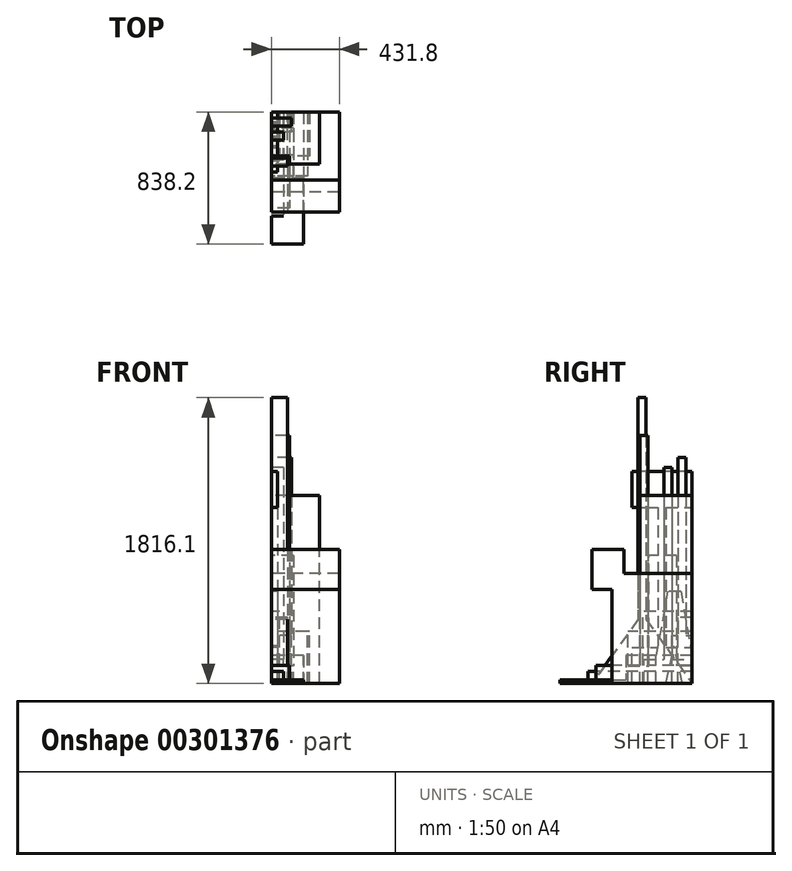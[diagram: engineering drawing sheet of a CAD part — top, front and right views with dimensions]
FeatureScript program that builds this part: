
annotation { "Feature Type Name" : "Feature", "Feature Type Description" : "" }
export const myFeature = defineFeature(function(context is Context, id is Id, definition is map)
    precondition{}
    {
        {
            var Q0;
            Q0=qCreatedBy(makeId("Right.planeOp"),FACE);
            var sketch = newSketch(context, id + "F0", { "sketchPlane" : qUnion([Q0])});
            skLineSegment(sketch, "E0.bottom", {"start": v(0, 0) * mm, "end": v(-508, 0) * mm});
            skLineSegment(sketch, "E0.top", {"start": v(0, 698.5) * mm, "end": v(-432.84, 698.5) * mm});
            skLineSegment(sketch, "E0.left", {"start": v(0, 0) * mm, "end": v(0, 698.5) * mm});
            skLineSegment(sketch, "E0.right", {"start": v(-508, 0) * mm, "end": v(-508, 597.32) * mm});
            skLineSegment(sketch, "E1.top", {"start": v(-432.84, 850.9) * mm, "end": v(-635, 850.9) * mm});
            skLineSegment(sketch, "E1.right", {"start": v(-635, 597.32) * mm, "end": v(-635, 850.9) * mm});
            skLineSegment(sketch, "E2", {"start": v(-432.84, 850.9) * mm, "end": v(-432.84, 698.5) * mm});
            skLineSegment(sketch, "E3", {"start": v(-635, 597.32) * mm, "end": v(-508, 597.32) * mm});
            skSolve(sketch);
        }
        {
            var Q0;
            Q0 = qSketchRegion(id + "F0", true);
            extrude(context, id + "F1", {"entities" : qUnion([Q0]), "depth" : 431.8 * mm});
        }
        {
            var Q0;
            Q0=qCreatedBy(makeId("Right.planeOp"),FACE);
            var sketch = newSketch(context, id + "F2", { "sketchPlane" : qUnion([Q0])});
            skLineSegment(sketch, "E4.bottom", {"start": v(0, 0) * mm, "end": v(-279.4, 0) * mm});
            skLineSegment(sketch, "E4.top", {"start": v(0, 330.2) * mm, "end": v(-279.4, 330.2) * mm});
            skLineSegment(sketch, "E4.left", {"start": v(0, 0) * mm, "end": v(0, 330.2) * mm});
            skLineSegment(sketch, "E4.right", {"start": v(-279.4, 0) * mm, "end": v(-279.4, 330.2) * mm});
            skSolve(sketch);
        }
        {
            var Q0;
            Q0 = qSketchRegion(id + "F2", true);
            extrude(context, id + "F3", {"entities" : qUnion([Q0]), "depth" : 241.3 * mm});
        }
        {
            var Q0;
            Q0=qCreatedBy(makeId("Right.planeOp"),FACE);
            var sketch = newSketch(context, id + "F4", { "sketchPlane" : qUnion([Q0])});
            skLineSegment(sketch, "E5.bottom", {"start": v(0, 0) * mm, "end": v(-88.9, 0) * mm});
            skLineSegment(sketch, "E5.top", {"start": v(0, 419.1) * mm, "end": v(-88.9, 419.1) * mm});
            skLineSegment(sketch, "E5.left", {"start": v(0, 0) * mm, "end": v(0, 419.1) * mm});
            skLineSegment(sketch, "E5.right", {"start": v(-88.9, 0) * mm, "end": v(-88.9, 419.1) * mm});
            skSolve(sketch);
        }
        {
            var Q0;
            Q0 = qSketchRegion(id + "F4", true);
            extrude(context, id + "F5", {"entities" : qUnion([Q0]), "depth" : 101.6 * mm});
        }
        {
            var Q0;
            Q0=qCreatedBy(makeId("Right.planeOp"),FACE);
            var sketch = newSketch(context, id + "F6", { "sketchPlane" : qUnion([Q0])});
            skLineSegment(sketch, "E6.bottom", {"start": v(0, 0) * mm, "end": v(-311.15, 0) * mm});
            skLineSegment(sketch, "E6.top", {"start": v(0, 457.2) * mm, "end": v(-311.15, 457.2) * mm});
            skLineSegment(sketch, "E6.left", {"start": v(0, 0) * mm, "end": v(0, 457.2) * mm});
            skLineSegment(sketch, "E6.right", {"start": v(-311.15, 0) * mm, "end": v(-311.15, 457.2) * mm});
            skSolve(sketch);
        }
        {
            var Q0;
            Q0 = qSketchRegion(id + "F6", true);
            extrude(context, id + "F7", {"entities" : qUnion([Q0]), "depth" : 50.8 * mm});
        }
        {
            var Q0;
            Q0=qCreatedBy(makeId("Right.planeOp"),FACE);
            var sketch = newSketch(context, id + "F8", { "sketchPlane" : qUnion([Q0])});
            skLineSegment(sketch, "E7.bottom", {"start": v(0, 0) * mm, "end": v(-609.6, 0) * mm});
            skLineSegment(sketch, "E7.top", {"start": v(-279.4, 1574.8) * mm, "end": v(-330.2, 1574.8) * mm});
            skLineSegment(sketch, "E7.left", {"start": v(0, 0) * mm, "end": v(0, 114.3) * mm});
            skLineSegment(sketch, "E7.right", {"start": v(-609.6, 0) * mm, "end": v(-609.6, 114.3) * mm});
            skLineSegment(sketch, "E8", {"start": v(0, 114.3) * mm, "end": v(-609.6, 114.3) * mm});
            skLineSegment(sketch, "E9", {"start": v(-304.8, 1574.8) * mm, "end": v(-304.8, 114.3) * mm, "construction": true});
            skLineSegment(sketch, "E10", {"start": v(-330.2, 1574.8) * mm, "end": v(-330.2, 114.3) * mm});
            skLineSegment(sketch, "E11.MirrorCS", {"start": v(-279.4, 1574.8) * mm, "end": v(-279.4, 114.3) * mm});
            skSolve(sketch);
        }
        {
            var Q0;
            Q0 = qSketchRegion(id + "F8", true);
            extrude(context, id + "F9", {"entities" : qUnion([Q0]), "depth" : 114.3 * mm});
        }
        {
            var Q0;
            Q0=qCreatedBy(makeId("Right.planeOp"),FACE);
            var sketch = newSketch(context, id + "F10", { "sketchPlane" : qUnion([Q0])});
            skLineSegment(sketch, "E12.bottom", {"start": v(0, 0) * mm, "end": v(-381, 0) * mm});
            skLineSegment(sketch, "E12.top", {"start": v(0, 1346.2) * mm, "end": v(-381, 1346.2) * mm});
            skLineSegment(sketch, "E12.left", {"start": v(0, 0) * mm, "end": v(0, 228.6) * mm});
            skLineSegment(sketch, "E12.right", {"start": v(-381, 0) * mm, "end": v(-381, 228.6) * mm});
            skLineSegment(sketch, "E13", {"start": v(-381, 673.1) * mm, "end": v(0, 673.1) * mm, "construction": true});
            skLineSegment(sketch, "E14", {"start": v(-190.5, 1346.2) * mm, "end": v(-190.5, 0) * mm, "construction": true});
            skLineSegment(sketch, "E15", {"start": v(-381, 228.6) * mm, "end": v(-215.9, 228.6) * mm});
            skLineSegment(sketch, "E16", {"start": v(-215.9, 1117.6) * mm, "end": v(-215.9, 0) * mm});
            skLineSegment(sketch, "E17.MirrorCS", {"start": v(-165.1, 1117.6) * mm, "end": v(-165.1, 0) * mm});
            skLineSegment(sketch, "E18.MirrorCS", {"start": v(-381, 1117.6) * mm, "end": v(-215.9, 1117.6) * mm});
            skPoint(sketch, "E19.orphan", {"position": v(-215.9, 1346.2) * mm});
            skPoint(sketch, "E20.orphan", {"position": v(-165.1, 1346.2) * mm});
            skLineSegment(sketch, "E21.trimOffspring", {"start": v(-165.1, 1117.6) * mm, "end": v(0, 1117.6) * mm});
            skLineSegment(sketch, "E22.trimOffspring", {"start": v(-165.1, 228.6) * mm, "end": v(0, 228.6) * mm});
            skLineSegment(sketch, "E23.trimOffspring", {"start": v(0, 1117.6) * mm, "end": v(0, 1346.2) * mm});
            skLineSegment(sketch, "E24.trimOffspring", {"start": v(-381, 1117.6) * mm, "end": v(-381, 1346.2) * mm});
            skSolve(sketch);
        }
        {
            var Q0;
            Q0 = qSketchRegion(id + "F10", true);
            extrude(context, id + "F11", {"entities" : qUnion([Q0]), "depth" : 38.1 * mm});
        }
        {
            var Q0;
            Q0=qCreatedBy(makeId("Right.planeOp"),FACE);
            var sketch = newSketch(context, id + "F12", { "sketchPlane" : qUnion([Q0])});
            skLineSegment(sketch, "E25.bottom", {"start": v(0, 0) * mm, "end": v(-635, 0) * mm});
            skLineSegment(sketch, "E25.top", {"start": v(-292.1, 1816.1) * mm, "end": v(-342.9, 1816.1) * mm});
            skLineSegment(sketch, "E26", {"start": v(-342.9, 406.4) * mm, "end": v(-292.1, 406.4) * mm});
            skLineSegment(sketch, "E27", {"start": v(-317.5, 1816.1) * mm, "end": v(-317.5, 406.4) * mm, "construction": true});
            skLineSegment(sketch, "E28", {"start": v(-342.9, 1816.1) * mm, "end": v(-342.9, 406.4) * mm});
            skLineSegment(sketch, "E29.MirrorCS", {"start": v(-292.1, 1816.1) * mm, "end": v(-292.1, 406.4) * mm});
            skPoint(sketch, "E30.orphan", {"position": v(0, 1816.1) * mm});
            skPoint(sketch, "E31.orphan", {"position": v(-635, 1816.1) * mm});
            skLineSegment(sketch, "E32", {"start": v(-342.9, 406.4) * mm, "end": v(-635, 0) * mm});
            skLineSegment(sketch, "E33", {"start": v(-292.1, 406.4) * mm, "end": v(0, 0) * mm});
            skPoint(sketch, "E34.orphan", {"position": v(0, 406.4) * mm});
            skPoint(sketch, "E25.right.end.orphan", {"position": v(-635, 406.4) * mm});
            skSolve(sketch);
        }
        {
            var Q0;
            Q0 = qSketchRegion(id + "F12", true);
            extrude(context, id + "F13", {"entities" : qUnion([Q0]), "depth" : 101.6 * mm});
        }
        {
            var Q0;
            Q0=qCreatedBy(makeId("Right.planeOp"),FACE);
            var sketch = newSketch(context, id + "F14", { "sketchPlane" : qUnion([Q0])});
            skLineSegment(sketch, "E35.bottom", {"start": v(0, 0) * mm, "end": v(-304.8, 0) * mm});
            skLineSegment(sketch, "E35.top", {"start": v(-127, 1371.6) * mm, "end": v(-177.8, 1371.6) * mm});
            skLineSegment(sketch, "E35.left", {"start": v(0, 0) * mm, "end": v(0, 152.4) * mm});
            skLineSegment(sketch, "E35.right", {"start": v(-304.8, 0) * mm, "end": v(-304.8, 152.4) * mm});
            skLineSegment(sketch, "E36", {"start": v(-304.8, 152.4) * mm, "end": v(0, 152.4) * mm});
            skLineSegment(sketch, "E37", {"start": v(-152.4, 1371.6) * mm, "end": v(-152.4, 778.95) * mm, "construction": true});
            skLineSegment(sketch, "E38", {"start": v(-177.8, 1371.6) * mm, "end": v(-177.8, 152.4) * mm});
            skLineSegment(sketch, "E39.MirrorCS", {"start": v(-127, 1371.6) * mm, "end": v(-127, 152.4) * mm});
            skPoint(sketch, "E40.orphan", {"position": v(-304.8, 1371.6) * mm});
            skPoint(sketch, "E41.orphan", {"position": v(0, 1371.6) * mm});
            skSolve(sketch);
        }
        {
            var Q0;
            Q0 = qSketchRegion(id + "F14", true);
            extrude(context, id + "F15", {"entities" : qUnion([Q0]), "depth" : 76.2 * mm});
        }
        {
            var Q0;
            Q0=qCreatedBy(makeId("Right.planeOp"),FACE);
            var sketch = newSketch(context, id + "F16", { "sketchPlane" : qUnion([Q0])});
            skLineSegment(sketch, "E42.bottom", {"start": v(0, 0) * mm, "end": v(-127, 0) * mm});
            skLineSegment(sketch, "E42.top", {"start": v(-38.1, 1435.1) * mm, "end": v(-88.9, 1435.1) * mm});
            skLineSegment(sketch, "E42.left", {"start": v(0, 0) * mm, "end": v(0, 304.8) * mm});
            skLineSegment(sketch, "E42.right", {"start": v(-127, 0) * mm, "end": v(-127, 304.8) * mm});
            skLineSegment(sketch, "E43", {"start": v(-127, 304.8) * mm, "end": v(-88.9, 304.8) * mm});
            skLineSegment(sketch, "E44", {"start": v(-63.5, 1435.1) * mm, "end": v(-63.5, 1125.6) * mm, "construction": true});
            skLineSegment(sketch, "E45", {"start": v(-88.9, 1435.1) * mm, "end": v(-88.9, 304.8) * mm});
            skLineSegment(sketch, "E46.MirrorCS", {"start": v(-38.1, 1435.1) * mm, "end": v(-38.1, 304.8) * mm});
            skPoint(sketch, "E47.orphan", {"position": v(-127, 1435.1) * mm});
            skPoint(sketch, "E48.orphan", {"position": v(0, 1435.1) * mm});
            skLineSegment(sketch, "E49.trimOffspring", {"start": v(-38.1, 304.8) * mm, "end": v(0, 304.8) * mm});
            skSolve(sketch);
        }
        {
            var Q0;
            Q0 = qSketchRegion(id + "F16", true);
            extrude(context, id + "F17", {"entities" : qUnion([Q0]), "depth" : 127 * mm});
        }
        {
            var Q0;
            Q0=qCreatedBy(makeId("Right.planeOp"),FACE);
            var sketch = newSketch(context, id + "F18", { "sketchPlane" : qUnion([Q0])});
            skLineSegment(sketch, "E50.bottom", {"start": v(0, 0) * mm, "end": v(-838.2, 0) * mm});
            skLineSegment(sketch, "E50.top", {"start": v(0, 177.8) * mm, "end": v(-419.1, 177.8) * mm});
            skLineSegment(sketch, "E50.left", {"start": v(0, 0) * mm, "end": v(0, 177.8) * mm});
            skLineSegment(sketch, "E50.right", {"start": v(-838.2, 0) * mm, "end": v(-838.2, 21.47) * mm});
            skLineSegment(sketch, "E51", {"start": v(-419.1, 177.8) * mm, "end": v(-419.1, 21.47) * mm});
            skLineSegment(sketch, "E52", {"start": v(-838.2, 21.47) * mm, "end": v(-419.1, 21.47) * mm});
            skPoint(sketch, "E53.orphan", {"position": v(-419.1, 0) * mm});
            skPoint(sketch, "E54.orphan", {"position": v(-838.2, 177.8) * mm});
            skSolve(sketch);
        }
        {
            var Q0;
            Q0 = qSketchRegion(id + "F18", true);
            extrude(context, id + "F19", {"entities" : qUnion([Q0]), "depth" : 203.2 * mm});
        }
        {
            var Q0;
            Q0=qCreatedBy(makeId("Right.planeOp"),FACE);
            var sketch = newSketch(context, id + "F20", { "sketchPlane" : qUnion([Q0])});
            skLineSegment(sketch, "E55.bottom", {"start": v(0, 0) * mm, "end": v(-406.4, 0) * mm});
            skLineSegment(sketch, "E55.top", {"start": v(0, 330.2) * mm, "end": v(-406.4, 330.2) * mm});
            skLineSegment(sketch, "E55.left", {"start": v(0, 0) * mm, "end": v(0, 330.2) * mm});
            skLineSegment(sketch, "E55.right", {"start": v(-406.4, 0) * mm, "end": v(-406.4, 330.2) * mm});
            skSolve(sketch);
        }
        {
            var Q0;
            Q0 = qSketchRegion(id + "F20", true);
            extrude(context, id + "F21", {"entities" : qUnion([Q0]), "depth" : 228.6 * mm});
        }
        {
            var Q0;
            Q0=qCreatedBy(makeId("Right.planeOp"),FACE);
            var sketch = newSketch(context, id + "F22", { "sketchPlane" : qUnion([Q0])});
            skLineSegment(sketch, "E56.bottom", {"start": v(0, 0) * mm, "end": v(-660.4, 0) * mm});
            skLineSegment(sketch, "E56.top", {"start": v(0, 76.2) * mm, "end": v(-660.4, 76.2) * mm});
            skLineSegment(sketch, "E56.left", {"start": v(0, 0) * mm, "end": v(0, 76.2) * mm});
            skLineSegment(sketch, "E56.right", {"start": v(-660.4, 0) * mm, "end": v(-660.4, 76.2) * mm});
            skSolve(sketch);
        }
        {
            var Q0;
            Q0 = qSketchRegion(id + "F22", true);
            extrude(context, id + "F23", {"entities" : qUnion([Q0]), "depth" : 76.2 * mm});
        }
        {
            var Q0;
            Q0=qCreatedBy(makeId("Right.planeOp"),FACE);
            var sketch = newSketch(context, id + "F24", { "sketchPlane" : qUnion([Q0])});
            skLineSegment(sketch, "E57.bottom", {"start": v(0, 0) * mm, "end": v(-406.4, 0) * mm});
            skLineSegment(sketch, "E57.top", {"start": v(-100.07, 812.8) * mm, "end": v(-273.67, 812.8) * mm});
            skLineSegment(sketch, "E57.left", {"start": v(0, 0) * mm, "end": v(0, 110.25) * mm});
            skLineSegment(sketch, "E57.right", {"start": v(-406.4, 0) * mm, "end": v(-406.4, 110.25) * mm});
            skLineSegment(sketch, "E58", {"start": v(-406.4, 110.25) * mm, "end": v(-273.67, 110.25) * mm});
            skLineSegment(sketch, "E59", {"start": v(0, 110.25) * mm, "end": v(-100.07, 110.25) * mm});
            skLineSegment(sketch, "E60", {"start": v(-273.67, 110.25) * mm, "end": v(-273.67, 812.8) * mm});
            skLineSegment(sketch, "E61", {"start": v(-100.07, 812.8) * mm, "end": v(-100.07, 110.25) * mm});
            skLineSegment(sketch, "E62.trimOffspring", {"start": v(-100.07, 110.25) * mm, "end": v(0, 110.25) * mm});
            skSolve(sketch);
        }
        {
            var Q0;
            Q0 = qSketchRegion(id + "F24", true);
            extrude(context, id + "F25", {"entities" : qUnion([Q0]), "depth" : 139.7 * mm});
        }
        {
            var Q0;
            Q0=qCreatedBy(makeId("Right.planeOp"),FACE);
            var sketch = newSketch(context, id + "F26", { "sketchPlane" : qUnion([Q0])});
            skLineSegment(sketch, "E63.bottom", {"start": v(0, 0) * mm, "end": v(-330.2, 0) * mm});
            skLineSegment(sketch, "E63.top", {"start": v(0, 1193.8) * mm, "end": v(-330.2, 1193.8) * mm});
            skLineSegment(sketch, "E63.left", {"start": v(0, 0) * mm, "end": v(0, 1193.8) * mm});
            skLineSegment(sketch, "E63.right", {"start": v(-330.2, 0) * mm, "end": v(-330.2, 1193.8) * mm});
            skSolve(sketch);
        }
        {
            var Q0;
            Q0=makeQuery(id+"F26.imprint","IMPRINT",FACE,{"disambiguationData":[TD([[makeQuery(id+"F26.imprint","IMPRINT",EDGE,{"derivedFrom":sQuery(id+"F26.wireOp",EDGE,"E63.bottom")}),-1.0]])]});
            extrude(context, id + "F27", {"entities" : qUnion([Q0]), "depth" : 304.8 * mm});
        }
        {
            var Q0;
            Q0=qCreatedBy(makeId("Right.planeOp"),FACE);
            var sketch = newSketch(context, id + "F28", { "sketchPlane" : qUnion([Q0])});
            skLineSegment(sketch, "E64.bottom", {"start": v(0, 0) * mm, "end": v(-62.38, 0) * mm});
            skLineSegment(sketch, "E64.top", {"start": v(-72.51, 584.2) * mm, "end": v(-156.09, 584.2) * mm});
            skLineSegment(sketch, "E64.left", {"start": v(0, 0) * mm, "end": v(0, 177.01) * mm});
            skLineSegment(sketch, "E64.right", {"start": v(-228.6, 0) * mm, "end": v(-228.6, 177.01) * mm});
            skLineSegment(sketch, "E65", {"start": v(-114.3, 584.2) * mm, "end": v(-114.3, 239.26) * mm, "construction": true});
            skLineSegment(sketch, "E66", {"start": v(-156.09, 584.2) * mm, "end": v(-228.6, 177.01) * mm});
            skLineSegment(sketch, "E67", {"start": v(-166.22, 0) * mm, "end": v(-114.3, 239.26) * mm});
            skPoint(sketch, "E68.orphan", {"position": v(-228.6, 584.2) * mm});
            skLineSegment(sketch, "E69.MirrorCS", {"start": v(-72.51, 584.2) * mm, "end": v(0, 177.01) * mm});
            skLineSegment(sketch, "E70.MirrorCS", {"start": v(-62.38, 0) * mm, "end": v(-114.3, 239.26) * mm});
            skPoint(sketch, "E71.orphan", {"position": v(0, 584.2) * mm});
            skLineSegment(sketch, "E72.trimOffspring", {"start": v(-166.22, 0) * mm, "end": v(-228.6, 0) * mm});
            skSolve(sketch);
        }
        {
            var Q0;
            Q0 = qSketchRegion(id + "F28", true);
            extrude(context, id + "F29", {"entities" : qUnion([Q0]), "depth" : 38.1 * mm});
        }
    });
